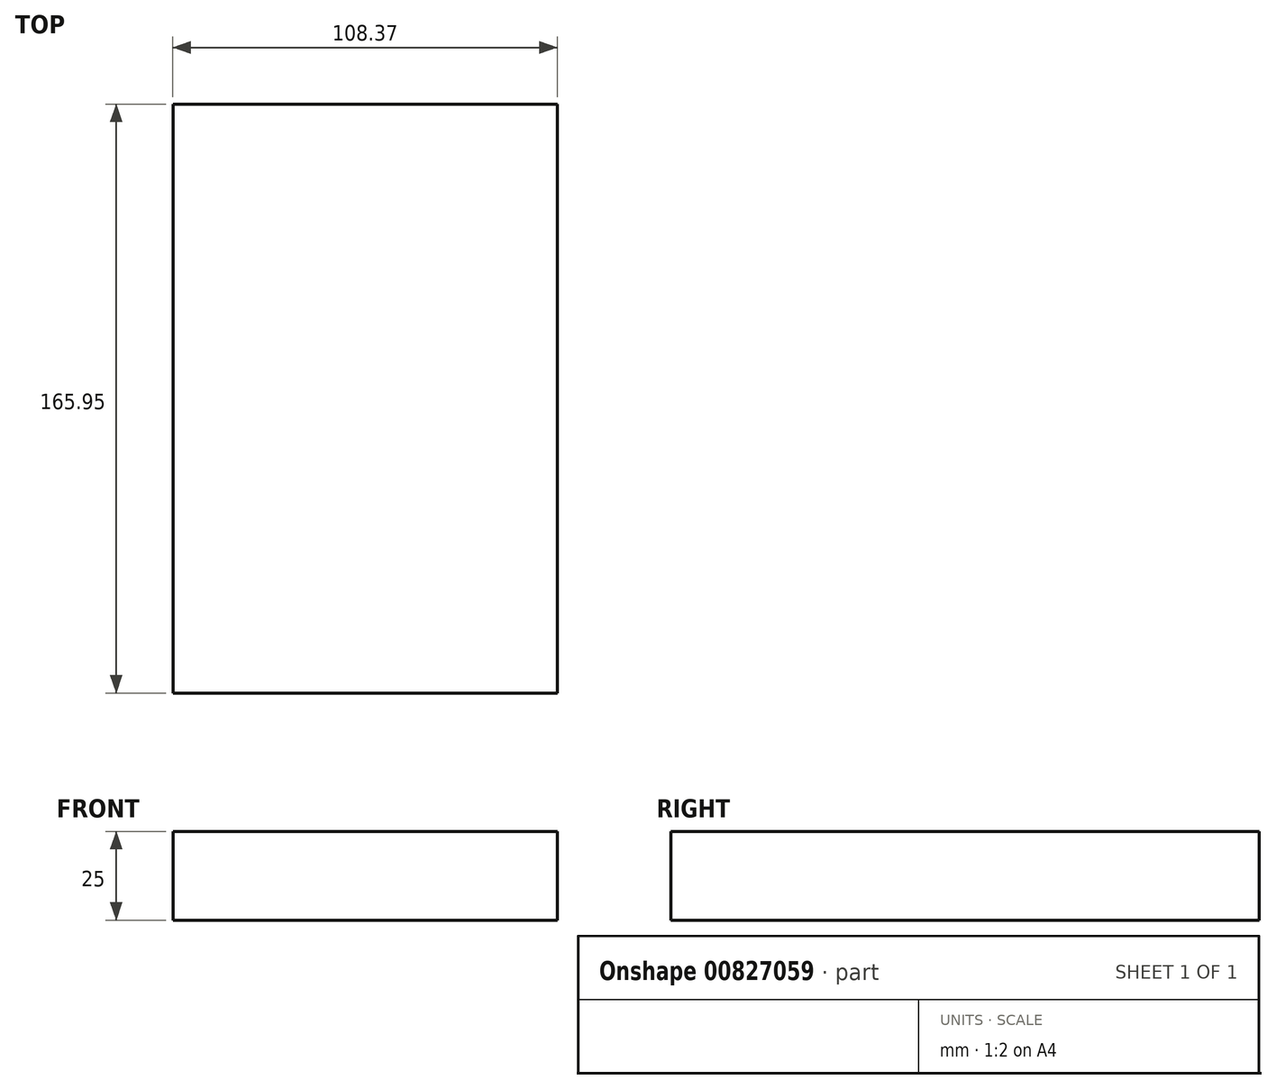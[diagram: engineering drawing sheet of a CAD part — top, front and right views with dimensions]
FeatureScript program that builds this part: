
annotation { "Feature Type Name" : "Feature", "Feature Type Description" : "" }
export const myFeature = defineFeature(function(context is Context, id is Id, definition is map)
    precondition{}
    {
        {
            var Q0;
            Q0=qCreatedBy(makeId("Top.planeOp"),FACE);
            var sketch = newSketch(context, id + "F0", { "sketchPlane" : qUnion([Q0])});
            skLineSegment(sketch, "E0.bottom", {"start": v(-61.92, -37.69) * mm, "end": v(46.45, -37.69) * mm});
            skLineSegment(sketch, "E0.top", {"start": v(-61.92, 128.26) * mm, "end": v(46.45, 128.26) * mm});
            skLineSegment(sketch, "E0.left", {"start": v(-61.92, -37.69) * mm, "end": v(-61.92, 128.26) * mm});
            skLineSegment(sketch, "E0.right", {"start": v(46.45, -37.69) * mm, "end": v(46.45, 128.26) * mm});
            skSolve(sketch);
        }
        {
            var Q0;
            Q0 = qSketchRegion(id + "F0", true);
            extrude(context, id + "F1", {"entities" : qUnion([Q0]), "depth" : 25 * mm, "offsetDistance" : 25 * mm});
        }
    });
